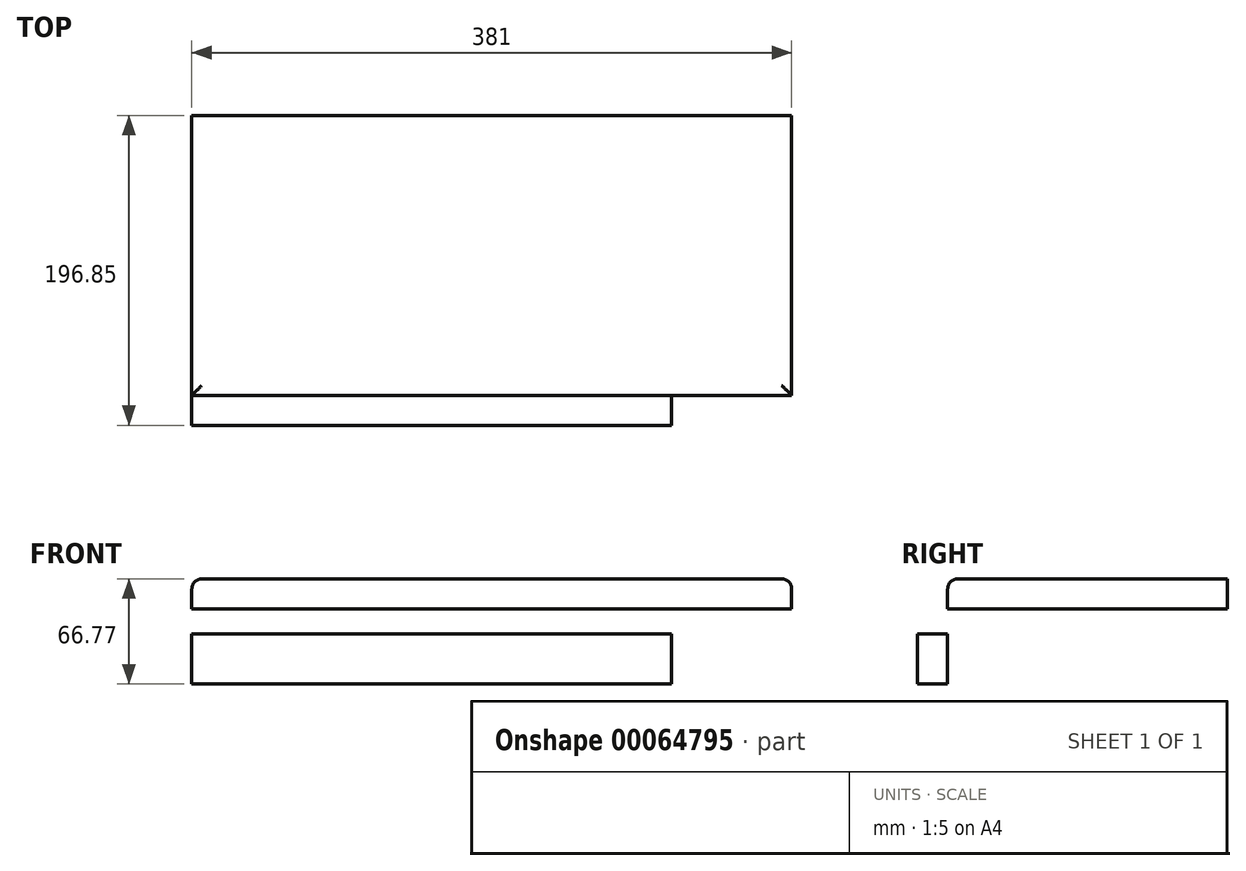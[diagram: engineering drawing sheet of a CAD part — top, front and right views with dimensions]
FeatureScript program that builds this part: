
annotation { "Feature Type Name" : "Feature", "Feature Type Description" : "" }
export const myFeature = defineFeature(function(context is Context, id is Id, definition is map)
    precondition{}
    {
        {
            var Q0;
            Q0=qCreatedBy(makeId("Top.planeOp"),FACE);
            var sketch = newSketch(context, id + "F0", { "sketchPlane" : qUnion([Q0])});
            skLineSegment(sketch, "E0.bottom", {"start": v(0, 0) * mm, "end": v(381, 0) * mm});
            skLineSegment(sketch, "E0.top", {"start": v(0, 177.8) * mm, "end": v(381, 177.8) * mm});
            skLineSegment(sketch, "E0.left", {"start": v(0, 0) * mm, "end": v(0, 177.8) * mm});
            skLineSegment(sketch, "E0.right", {"start": v(381, 0) * mm, "end": v(381, 177.8) * mm});
            skSolve(sketch);
        }
        {
            var Q0;
            Q0=makeQuery(id+"F0.imprint","IMPRINT",FACE,{"disambiguationData":[TD([[makeQuery(id+"F0.imprint","IMPRINT",EDGE,{"derivedFrom":sQuery(id+"F0.wireOp",EDGE,"E0.bottom")}),1.0]])]});
            extrude(context, id + "F1", {"entities" : qUnion([Q0]), "depth" : 19.05 * mm});
        }
        {
            var Q0;
            Q0=makeQuery(id+"F1.opExtrude","CAP_EDGE",EDGE,{"disambiguationData":[OSD([sQuery(id+"F0.wireOp",EDGE,"E0.left")])],"isStart":false});
            var Q1;
            Q1=makeQuery(id+"F1.opExtrude","CAP_EDGE",EDGE,{"disambiguationData":[OSD([sQuery(id+"F0.wireOp",EDGE,"E0.bottom")])],"isStart":false});
            var Q2;
            Q2=makeQuery(id+"F1.opExtrude","CAP_EDGE",EDGE,{"disambiguationData":[OSD([sQuery(id+"F0.wireOp",EDGE,"E0.right")])],"isStart":false});
            fillet(context, id + "F2", {"entities" : qUnion([Q0, Q1, Q2]), "radius" : 6.35 * mm, "tangentPropagation" : true, "allowEdgeOverflow" : false});
        }
        {
            var Q0;
            Q0=qCreatedBy(makeId("Front.planeOp"),FACE);
            var sketch = newSketch(context, id + "F3", { "sketchPlane" : qUnion([Q0])});
            skLineSegment(sketch, "E1.bottom", {"start": v(0, -47.72) * mm, "end": v(304.8, -47.72) * mm});
            skLineSegment(sketch, "E1.top", {"start": v(0, -15.97) * mm, "end": v(304.8, -15.97) * mm});
            skLineSegment(sketch, "E1.left", {"start": v(0, -47.72) * mm, "end": v(0, -15.97) * mm});
            skLineSegment(sketch, "E1.right", {"start": v(304.8, -47.72) * mm, "end": v(304.8, -15.97) * mm});
            skSolve(sketch);
        }
        {
            var Q0;
            Q0=makeQuery(id+"F3.imprint","IMPRINT",FACE,{"disambiguationData":[TD([[makeQuery(id+"F3.imprint","IMPRINT",EDGE,{"derivedFrom":sQuery(id+"F3.wireOp",EDGE,"E1.bottom")}),1.0]])]});
            extrude(context, id + "F4", {"entities" : qUnion([Q0]), "depth" : 19.05 * mm});
        }
    });
